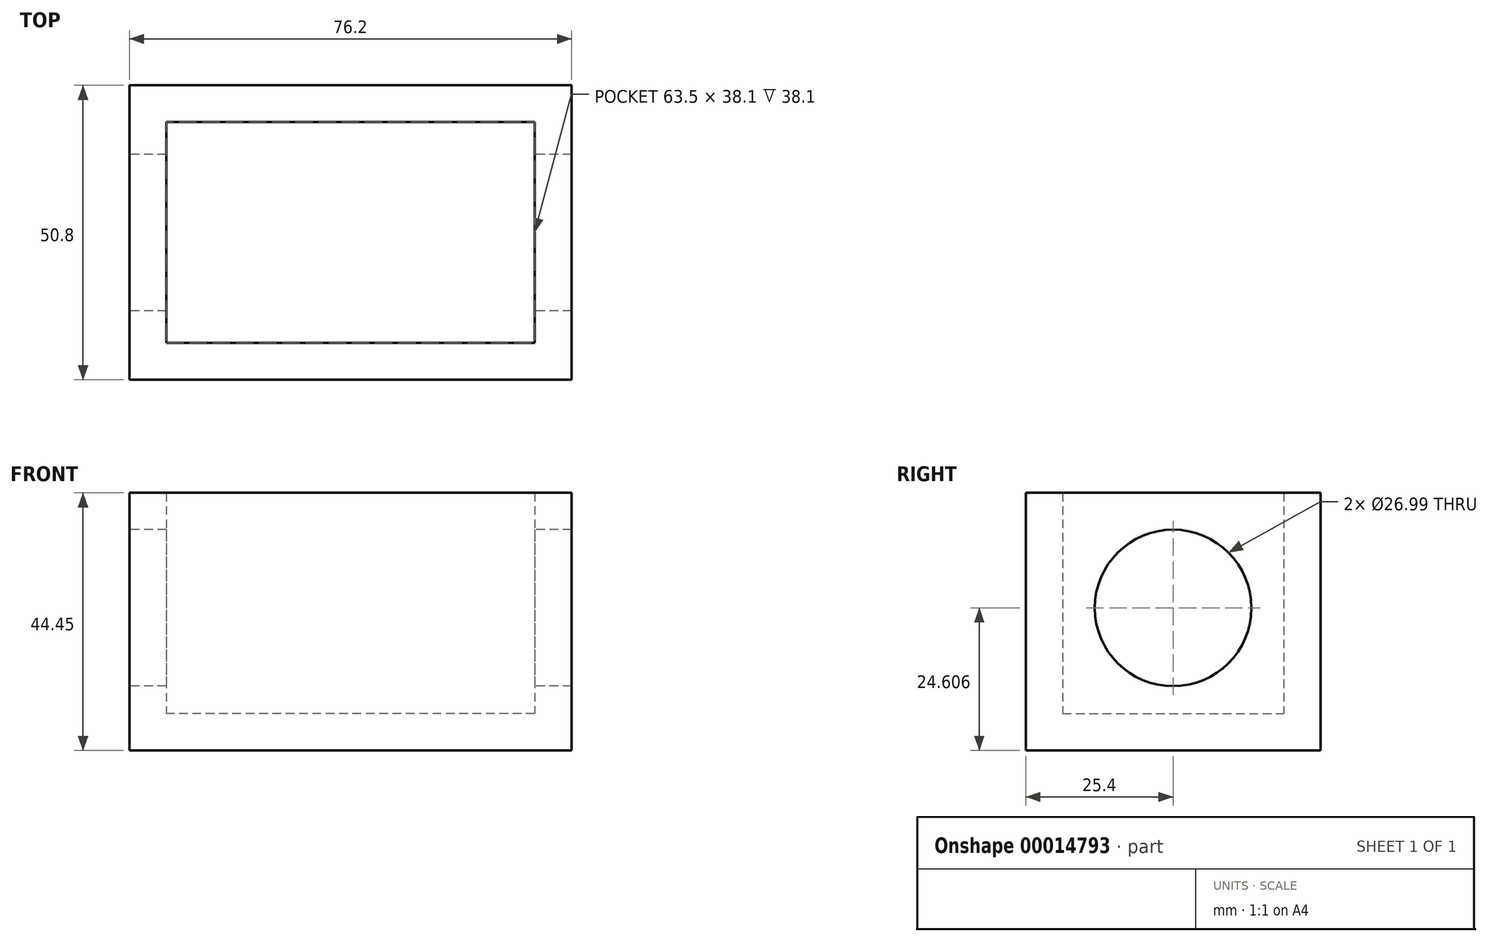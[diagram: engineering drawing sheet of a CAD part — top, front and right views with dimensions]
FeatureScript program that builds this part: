
annotation { "Feature Type Name" : "Feature", "Feature Type Description" : "" }
export const myFeature = defineFeature(function(context is Context, id is Id, definition is map)
    precondition{}
    {
        {
            var Q0;
            Q0=qCreatedBy(makeId("Top.planeOp"),FACE);
            var sketch = newSketch(context, id + "F0", { "sketchPlane" : qUnion([Q0])});
            skLineSegment(sketch, "E0.rect.bottom", {"start": v(38.1, -25.4) * mm, "end": v(-38.1, -25.4) * mm});
            skLineSegment(sketch, "E0.rect.top", {"start": v(38.1, 25.4) * mm, "end": v(-38.1, 25.4) * mm});
            skLineSegment(sketch, "E0.rect.left", {"start": v(38.1, -25.4) * mm, "end": v(38.1, 25.4) * mm});
            skLineSegment(sketch, "E0.rect.right", {"start": v(-38.1, -25.4) * mm, "end": v(-38.1, 25.4) * mm});
            skPoint(sketch, "E0.rect.middle", {"position": v(0, 0) * mm});
            skSolve(sketch);
        }
        {
            var Q0;
            Q0 = qSketchRegion(id + "F0", true);
            extrude(context, id + "F1", {"entities" : qUnion([Q0]), "depth" : 6.35 * mm});
        }
        {
            var Q0;
            Q0=makeQuery(id+"F1.opExtrude","CAP_FACE",FACE,{"disambiguationData":[OSD([sQuery(id+"F0.wireOp",EDGE,"E0.rect.bottom"),sQuery(id+"F0.wireOp",EDGE,"E0.rect.top"),sQuery(id+"F0.wireOp",EDGE,"E0.rect.left"),sQuery(id+"F0.wireOp",EDGE,"E0.rect.right")])],"isStart":false});
            var sketch = newSketch(context, id + "F2", { "sketchPlane" : qUnion([Q0])});
            skLineSegment(sketch, "E1.rect.bottom", {"start": v(38.1, -25.4) * mm, "end": v(-38.1, -25.4) * mm});
            skLineSegment(sketch, "E1.rect.top", {"start": v(38.1, 25.4) * mm, "end": v(-38.1, 25.4) * mm});
            skLineSegment(sketch, "E1.rect.left", {"start": v(38.1, -25.4) * mm, "end": v(38.1, 25.4) * mm});
            skLineSegment(sketch, "E1.rect.right", {"start": v(-38.1, -25.4) * mm, "end": v(-38.1, 25.4) * mm});
            skPoint(sketch, "E1.rect.middle", {"position": v(0, 0) * mm});
            skLineSegment(sketch, "E2.rect.bottom", {"start": v(31.75, -19.05) * mm, "end": v(-31.75, -19.05) * mm});
            skLineSegment(sketch, "E2.rect.top", {"start": v(31.75, 19.05) * mm, "end": v(-31.75, 19.05) * mm});
            skLineSegment(sketch, "E2.rect.left", {"start": v(31.75, -19.05) * mm, "end": v(31.75, 19.05) * mm});
            skLineSegment(sketch, "E2.rect.right", {"start": v(-31.75, -19.05) * mm, "end": v(-31.75, 19.05) * mm});
            skSolve(sketch);
        }
        {
            var Q0;
            Q0=makeQuery(id+"F2.imprint","IMPRINT",FACE,{"disambiguationData":[TD([[makeQuery(id+"F2.imprint","IMPRINT",EDGE,{"derivedFrom":sQuery(id+"F2.wireOp",EDGE,"E1.rect.bottom")}),-1.0]])]});
            extrude(context, id + "F3", {"entities" : qUnion([Q0]), "operationType" : NewBodyOperationType.ADD, "depth" : 38.1 * mm});
        }
        {
            var Q0;
            Q0=makeQuery(id+"F3.boolean.opBoolean","MERGE",FACE,{"derivedFrom":[makeQuery(id+"F1.opExtrude","SWEPT_FACE",FACE,{"disambiguationData":[OSD([sQuery(id+"F0.wireOp",EDGE,"E0.rect.right")])]}),makeQuery(id+"F3.opExtrude","SWEPT_FACE",FACE,{"disambiguationData":[OSD([sQuery(id+"F2.wireOp",EDGE,"E1.rect.right")])]})]});
            var sketch = newSketch(context, id + "F4", { "sketchPlane" : qUnion([Q0])});
            skCircle(sketch, "E3", {"center": v(0, 24.6) * mm, "radius": 13.5 * mm});
            skSolve(sketch);
        }
        {
            var Q0;
            Q0=makeQuery(id+"F4.imprint","IMPRINT",FACE,{"disambiguationData":[TD([[makeQuery(id+"F4.imprint","IMPRINT",EDGE,{"derivedFrom":sQuery(id+"F4.wireOp",EDGE,"E3")}),1.0]])]});
            var Q1;
            Q1=sQuery(id+"F4.wireOp",EDGE,"E3");
            extrude(context, id + "F5", {"entities" : qUnion([Q0]), "operationType" : NewBodyOperationType.REMOVE, "surfaceEntities" : qUnion([Q1]), "oppositeDirection" : true, "depth" : 111.15 * mm});
        }
    });
